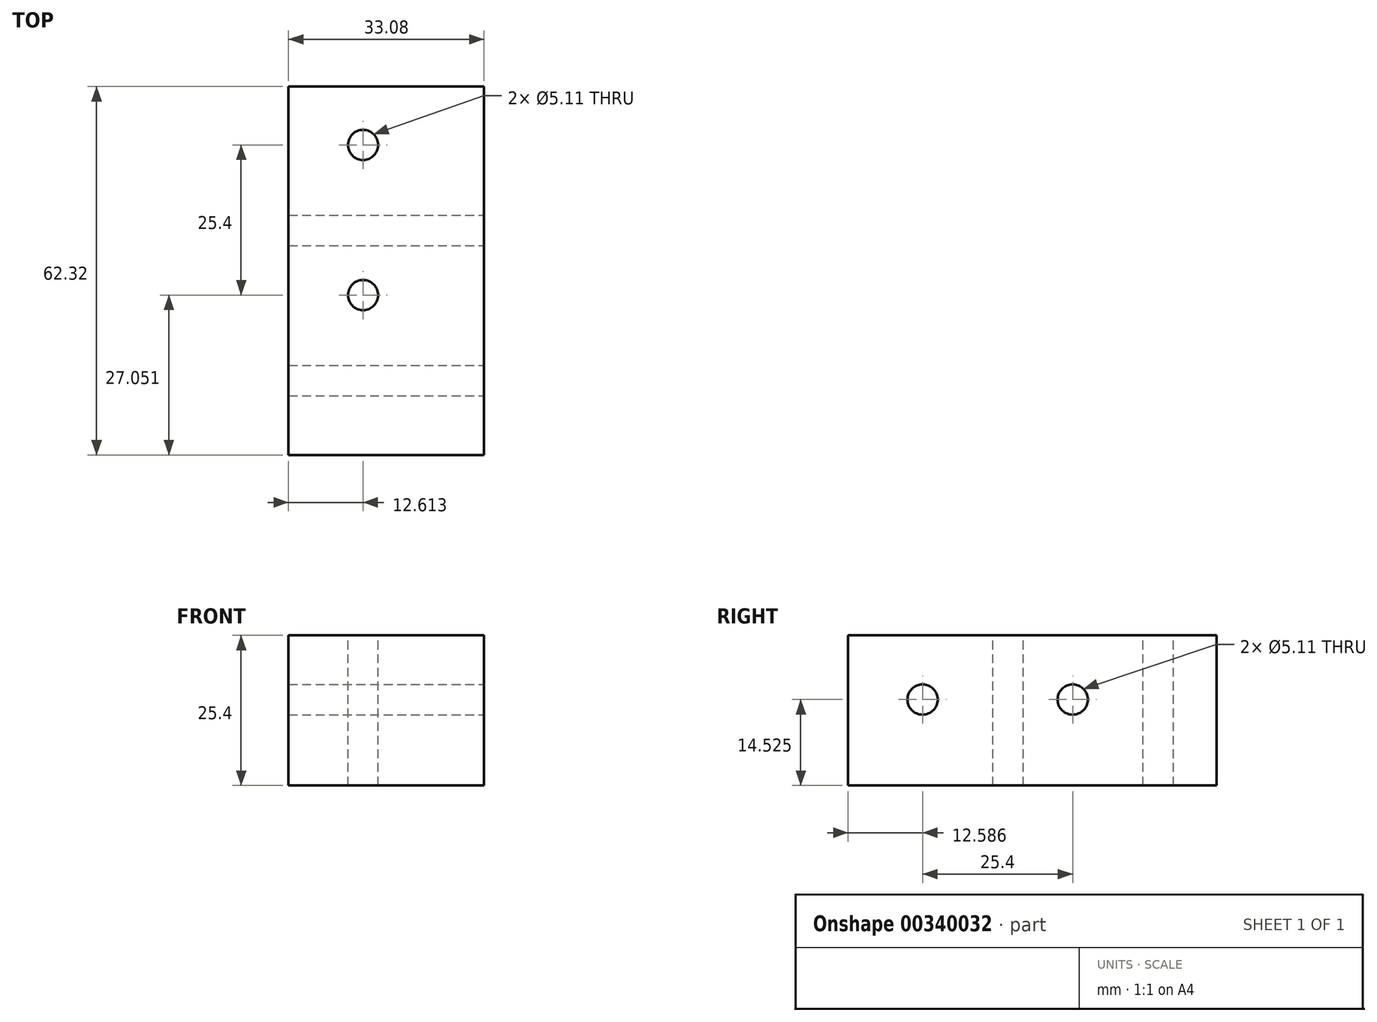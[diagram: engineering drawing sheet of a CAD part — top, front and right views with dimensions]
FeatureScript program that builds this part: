
annotation { "Feature Type Name" : "Feature", "Feature Type Description" : "" }
export const myFeature = defineFeature(function(context is Context, id is Id, definition is map)
    precondition{}
    {
        {
            var Q0;
            Q0=qCreatedBy(makeId("Top.planeOp"),FACE);
            var sketch = newSketch(context, id + "F0", { "sketchPlane" : qUnion([Q0])});
            skLineSegment(sketch, "E0.bottom", {"start": v(-26.77, 19.76) * mm, "end": v(6.3, 19.76) * mm});
            skLineSegment(sketch, "E0.top", {"start": v(-26.77, -42.56) * mm, "end": v(6.3, -42.56) * mm});
            skLineSegment(sketch, "E0.left", {"start": v(-26.77, 19.76) * mm, "end": v(-26.77, -42.56) * mm});
            skLineSegment(sketch, "E0.right", {"start": v(6.3, 19.76) * mm, "end": v(6.3, -42.56) * mm});
            skSolve(sketch);
        }
        {
            var Q0;
            Q0=makeQuery(id+"F0.imprint","IMPRINT",FACE,{"disambiguationData":[TD([[makeQuery(id+"F0.imprint","IMPRINT",EDGE,{"derivedFrom":sQuery(id+"F0.wireOp",EDGE,"E0.bottom")}),-1.0]])]});
            extrude(context, id + "F1", {"entities" : qUnion([Q0]), "depth" : 25.4 * mm});
        }
        {
            var Q0;
            Q0=makeQuery(id+"F1.opExtrude","CAP_FACE",FACE,{"disambiguationData":[OSD([sQuery(id+"F0.wireOp",EDGE,"E0.bottom"),sQuery(id+"F0.wireOp",EDGE,"E0.top"),sQuery(id+"F0.wireOp",EDGE,"E0.left"),sQuery(id+"F0.wireOp",EDGE,"E0.right")])],"isStart":false});
            var sketch = newSketch(context, id + "F2", { "sketchPlane" : qUnion([Q0])});
            skCircle(sketch, "E1", {"center": v(-14.16, 9.9) * mm, "radius": 4.7 * mm});
            skCircle(sketch, "E2.0.1.0", {"center": v(-14.16, -15.5) * mm, "radius": 4.7 * mm});
            skLineSegment(sketch, "E2.direction1", {"start": v(-14.16, 9.9) * mm, "end": v(11.24, 9.9) * mm, "construction": true});
            skLineSegment(sketch, "E2.direction2", {"start": v(-14.16, 9.9) * mm, "end": v(-14.16, -15.5) * mm, "construction": true});
            skSolve(sketch);
        }
        {
            var Q0;
            Q0=makeQuery(id+"F1.opExtrude","SWEPT_FACE",FACE,{"disambiguationData":[OSD([sQuery(id+"F0.wireOp",EDGE,"E0.right")])]});
            var sketch = newSketch(context, id + "F3", { "sketchPlane" : qUnion([Q0])});
            skCircle(sketch, "E3", {"center": v(-29.97, 14.53) * mm, "radius": 2.4 * mm});
            skCircle(sketch, "E4.1.0.0", {"center": v(-4.57, 14.53) * mm, "radius": 2.4 * mm});
            skLineSegment(sketch, "E4.direction1", {"start": v(-29.97, 14.53) * mm, "end": v(-4.57, 14.53) * mm, "construction": true});
            skSolve(sketch);
        }
        {
            var Q0;
            Q0=sQuery(id+"F3.wireOp",VERTEX,"E3.center");
            var Q1;
            Q1=sQuery(id+"F3.wireOp",VERTEX,"E4.1.0.0.center");
            var Q2;
            Q2=makeQuery(id+"F1.opExtrude","SWEPT_BODY",BODY,{"disambiguationData":[OSD([sQuery(id+"F0.wireOp",EDGE,"E0.bottom"),sQuery(id+"F0.wireOp",EDGE,"E0.top"),sQuery(id+"F0.wireOp",EDGE,"E0.left"),sQuery(id+"F0.wireOp",EDGE,"E0.right")])]});
            hole(context, id + "F4", {"style" : HoleStyle.SIMPLE, "endStyle" : HoleEndStyle.THROUGH, "holeDiameter" : 5.1 * mm, "tappedDepth" : 12.7 * mm, "tapClearance" : 3, "locations" : qUnion([Q0, Q1]), "scope" : qUnion([Q2])});
        }
        {
            var Q0;
            Q0=sQuery(id+"F2.wireOp",VERTEX,"E1.center");
            var Q1;
            Q1=sQuery(id+"F2.wireOp",VERTEX,"E2.0.1.0.center");
            var Q2;
            Q2=makeQuery(id+"F1.opExtrude","SWEPT_BODY",BODY,{"disambiguationData":[OSD([sQuery(id+"F0.wireOp",EDGE,"E0.bottom"),sQuery(id+"F0.wireOp",EDGE,"E0.top"),sQuery(id+"F0.wireOp",EDGE,"E0.left"),sQuery(id+"F0.wireOp",EDGE,"E0.right")])]});
            hole(context, id + "F5", {"style" : HoleStyle.SIMPLE, "endStyle" : HoleEndStyle.THROUGH, "holeDiameter" : 5.1 * mm, "tappedDepth" : 12.7 * mm, "tapClearance" : 3, "locations" : qUnion([Q0, Q1]), "scope" : qUnion([Q2])});
        }
    });
